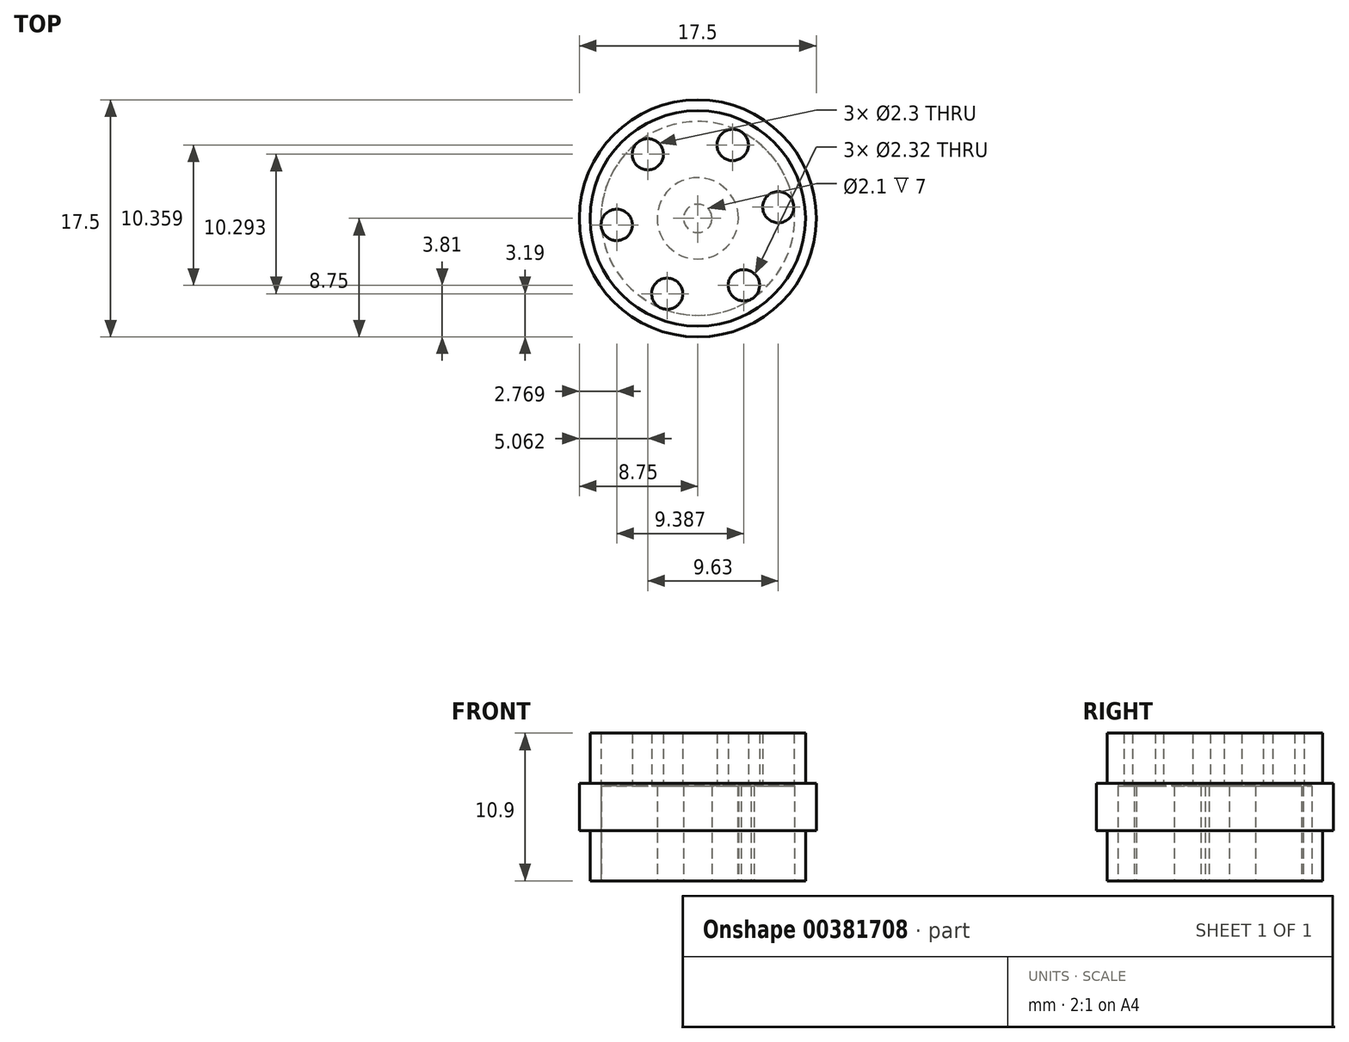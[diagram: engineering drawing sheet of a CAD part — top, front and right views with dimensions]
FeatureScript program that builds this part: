
annotation { "Feature Type Name" : "Feature", "Feature Type Description" : "" }
export const myFeature = defineFeature(function(context is Context, id is Id, definition is map)
    precondition{}
    {
        {
            var Q0;
            Q0=qCreatedBy(makeId("Top.planeOp"),FACE);
            var sketch = newSketch(context, id + "F0", { "sketchPlane" : qUnion([Q0])});
            skCircle(sketch, "E0", {"center": v(0, 0) * mm, "radius": 7.95 * mm});
            skSolve(sketch);
        }
        {
            var Q0;
            Q0 = qSketchRegion(id + "F0", true);
            extrude(context, id + "F1", {"entities" : qUnion([Q0]), "oppositeDirection" : true, "depth" : 3.7 * mm});
        }
        {
            var Q0;
            Q0=makeQuery(id+"F1.opExtrude","CAP_FACE",FACE,{"disambiguationData":[OSD([sQuery(id+"F0.wireOp",EDGE,"E0")])],"isStart":false});
            var sketch = newSketch(context, id + "F2", { "sketchPlane" : qUnion([Q0])});
            skCircle(sketch, "E1", {"center": v(0, 0) * mm, "radius": 8.75 * mm});
            skSolve(sketch);
        }
        {
            var Q0;
            Q0 = qSketchRegion(id + "F2", true);
            extrude(context, id + "F3", {"entities" : qUnion([Q0]), "operationType" : NewBodyOperationType.ADD, "depth" : 3.5 * mm});
        }
        {
            var Q0;
            Q0=makeQuery(id+"F3.opExtrude","CAP_FACE",FACE,{"disambiguationData":[OSD([sQuery(id+"F2.wireOp",EDGE,"E1")])],"isStart":false});
            var sketch = newSketch(context, id + "F4", { "sketchPlane" : qUnion([Q0])});
            skCircle(sketch, "E2", {"center": v(0, 0) * mm, "radius": 7.95 * mm});
            skSolve(sketch);
        }
        {
            var Q0;
            Q0 = qSketchRegion(id + "F4", true);
            extrude(context, id + "F5", {"entities" : qUnion([Q0]), "operationType" : NewBodyOperationType.ADD, "depth" : 3.7 * mm});
        }
        {
            var Q0;
            Q0=makeQuery(id+"F5.opExtrude","CAP_FACE",FACE,{"disambiguationData":[OSD([sQuery(id+"F4.wireOp",EDGE,"E2")])],"isStart":false});
            var sketch = newSketch(context, id + "F6", { "sketchPlane" : qUnion([Q0])});
            skCircle(sketch, "E3", {"center": v(0, 0) * mm, "radius": 6 * mm, "construction": true});
            skCircle(sketch, "E4", {"center": v(3.4, 4.94) * mm, "radius": 1.16 * mm});
            skCircle(sketch, "E5.1.0", {"center": v(-5.98, 0.48) * mm, "radius": 1.16 * mm});
            skCircle(sketch, "E5.2.0", {"center": v(2.57, -5.42) * mm, "radius": 1.16 * mm});
            skSolve(sketch);
        }
        {
            var Q0;
            Q0=makeQuery(id+"F6.imprint","IMPRINT",FACE,{"disambiguationData":[TD([[makeQuery(id+"F6.imprint","IMPRINT",EDGE,{"derivedFrom":sQuery(id+"F6.wireOp",EDGE,"E5.1.0")}),1.0]])]});
            var Q1;
            Q1=makeQuery(id+"F6.imprint","IMPRINT",FACE,{"disambiguationData":[TD([[makeQuery(id+"F6.imprint","IMPRINT",EDGE,{"derivedFrom":sQuery(id+"F6.wireOp",EDGE,"E5.2.0")}),1.0]])]});
            var Q2;
            Q2=makeQuery(id+"F6.imprint","IMPRINT",FACE,{"disambiguationData":[TD([[makeQuery(id+"F6.imprint","IMPRINT",EDGE,{"derivedFrom":sQuery(id+"F6.wireOp",EDGE,"E4")}),1.0]])]});
            extrude(context, id + "F7", {"entities" : qUnion([Q0, Q1, Q2]), "operationType" : NewBodyOperationType.REMOVE, "oppositeDirection" : true, "depth" : 25 * mm});
        }
        {
            var Q0;
            Q0=makeQuery(id+"F5.opExtrude","CAP_FACE",FACE,{"disambiguationData":[OSD([sQuery(id+"F4.wireOp",EDGE,"E2")])],"isStart":false});
            var sketch = newSketch(context, id + "F8", { "sketchPlane" : qUnion([Q0])});
            skCircle(sketch, "E6", {"center": v(0, 0) * mm, "radius": 6 * mm, "construction": true});
            skCircle(sketch, "E7", {"center": v(-2.26, 5.56) * mm, "radius": 1.15 * mm});
            skCircle(sketch, "E8.1.0", {"center": v(-3.69, -4.73) * mm, "radius": 1.15 * mm});
            skCircle(sketch, "E8.2.0", {"center": v(5.94, -0.83) * mm, "radius": 1.15 * mm});
            skSolve(sketch);
        }
        {
            var Q0;
            Q0=makeQuery(id+"F8.imprint","IMPRINT",FACE,{"disambiguationData":[TD([[makeQuery(id+"F8.imprint","IMPRINT",EDGE,{"derivedFrom":sQuery(id+"F8.wireOp",EDGE,"E7")}),1.0]])]});
            var Q1;
            Q1=makeQuery(id+"F8.imprint","IMPRINT",FACE,{"disambiguationData":[TD([[makeQuery(id+"F8.imprint","IMPRINT",EDGE,{"derivedFrom":sQuery(id+"F8.wireOp",EDGE,"E8.2.0")}),1.0]])]});
            var Q2;
            Q2=makeQuery(id+"F8.imprint","IMPRINT",FACE,{"disambiguationData":[TD([[makeQuery(id+"F8.imprint","IMPRINT",EDGE,{"derivedFrom":sQuery(id+"F8.wireOp",EDGE,"E8.1.0")}),1.0]])]});
            extrude(context, id + "F9", {"entities" : qUnion([Q0, Q1, Q2]), "operationType" : NewBodyOperationType.REMOVE, "oppositeDirection" : true, "depth" : 25 * mm});
        }
        {
            var Q0;
            Q0=makeQuery(id+"F5.opExtrude","CAP_FACE",FACE,{"disambiguationData":[OSD([sQuery(id+"F4.wireOp",EDGE,"E2")])],"isStart":false});
            var sketch = newSketch(context, id + "F10", { "sketchPlane" : qUnion([Q0])});
            skCircle(sketch, "E9", {"center": v(0, 0) * mm, "radius": 1.05 * mm});
            skCircle(sketch, "E10", {"center": v(0, 0) * mm, "radius": 3 * mm});
            skCircle(sketch, "E11", {"center": v(0, 0) * mm, "radius": 7.15 * mm});
            skSolve(sketch);
        }
        {
            var Q0;
            Q0 = qSketchRegion(id + "F10", true);
            var Q1;
            Q1=makeQuery(id+"F10.imprint","IMPRINT",FACE,{"disambiguationData":[TD([[makeQuery(id+"F10.imprint","IMPRINT",EDGE,{"derivedFrom":sQuery(id+"F10.wireOp",EDGE,"E9")}),1.0]])]});
            extrude(context, id + "F11", {"entities" : qUnion([Q0, Q1]), "operationType" : NewBodyOperationType.REMOVE, "oppositeDirection" : true, "depth" : 7 * mm});
        }
    });
